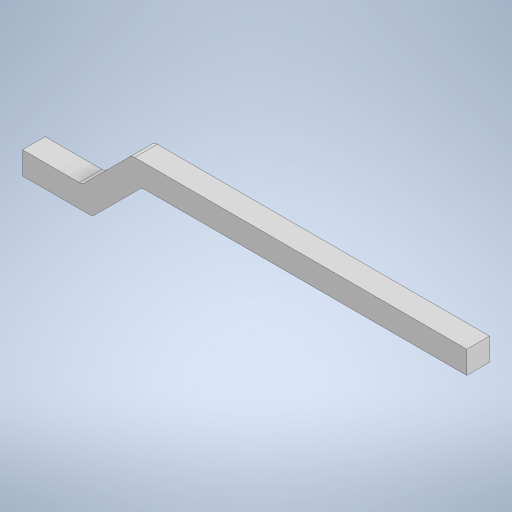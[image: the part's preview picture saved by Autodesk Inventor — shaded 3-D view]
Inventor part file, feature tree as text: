
AUTODESK INVENTOR PART (.ipt)
format: ipt  version: 2023 (Build 270158000, 158)  size: 240,128 bytes
history: native  units: mm
features: extrude x1, fillet x1, sketch x1
ambient origin geometry x8: Origin, YZ Plane, XZ Plane, XY Plane, X Axis, Y Axis, Z Axis, Center Point
bodies: Volumenkörper1 (feature_tree)
feature tree (3):
  extrude  "Extrusion1"  Depth=2.0mm
  fillet  "Rundung1"  Radius=9.3mm
  sketch  "Skizze1"  dims[d0=2.0mm d1=2.0mm d2=9.3mm d3=0.65mm d4=0.65mm d5=135.0deg d6=0.665mm d7=0.65mm d8=0.0mm d9=0.2mm]
